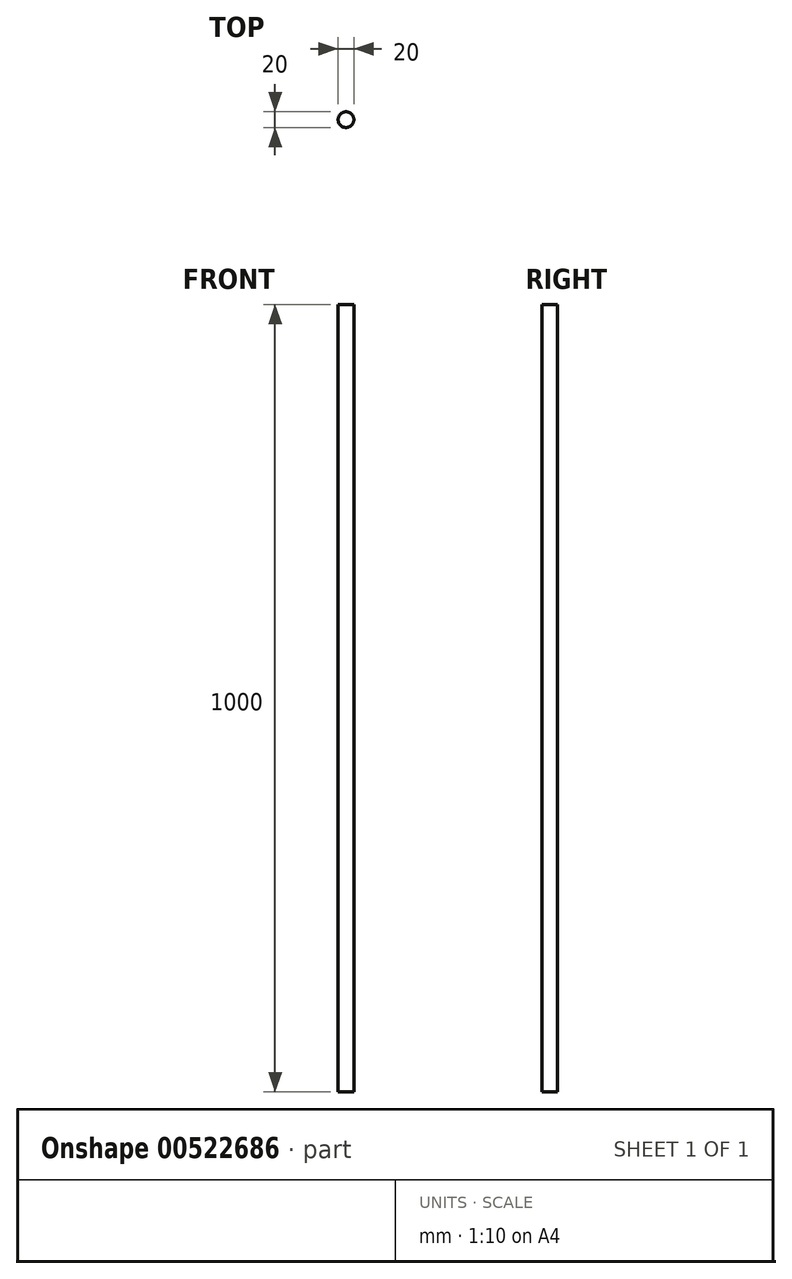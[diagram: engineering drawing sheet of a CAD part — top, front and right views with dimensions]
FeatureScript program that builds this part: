
annotation { "Feature Type Name" : "Feature", "Feature Type Description" : "" }
export const myFeature = defineFeature(function(context is Context, id is Id, definition is map)
    precondition{}
    {
        {
            var Q0;
            Q0=qCreatedBy(makeId("Top.planeOp"),FACE);
            var sketch = newSketch(context, id + "F0", { "sketchPlane" : qUnion([Q0])});
            skCircle(sketch, "E0", {"center": v(0, 0) * mm, "radius": 10 * mm});
            skSolve(sketch);
        }
        {
            var Q0;
            Q0=qSketchRegion(id+"F0",true);
            extrude(context, id + "F1", {"entities" : qUnion([Q0]), "depth" : 1000 * mm, "offsetDistance" : 25 * mm});
        }
    });
